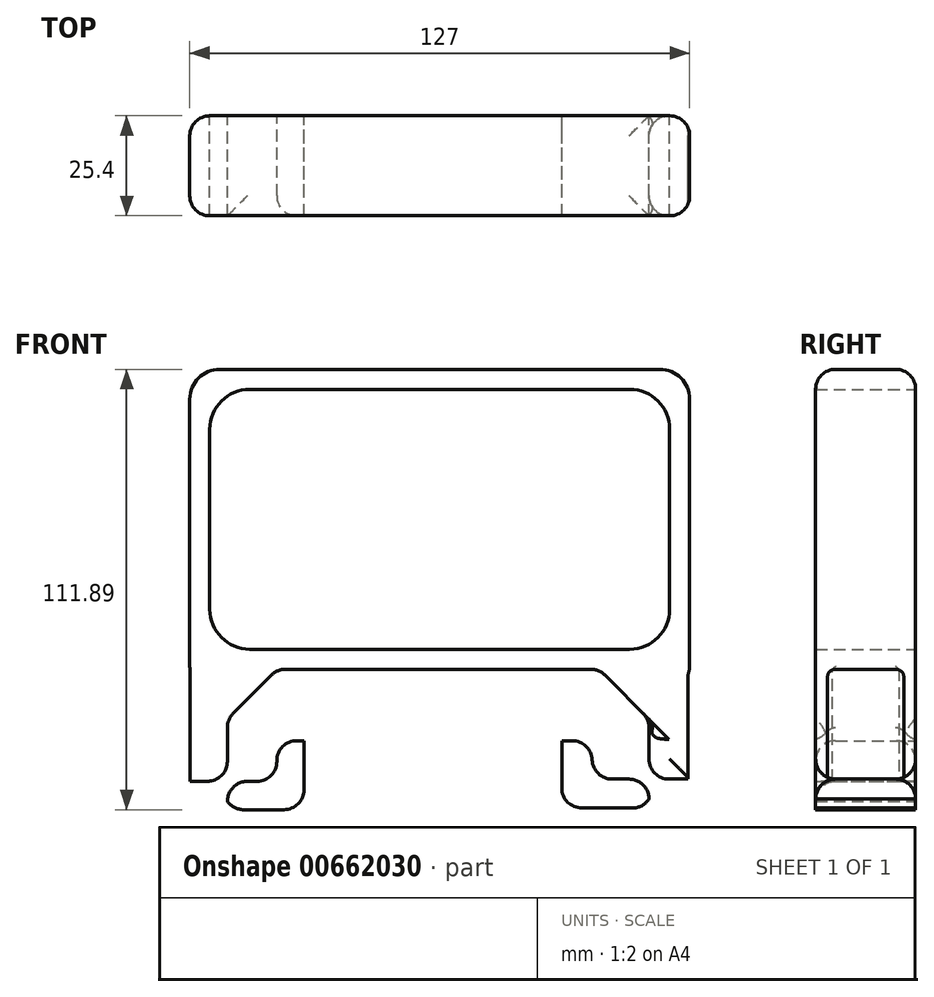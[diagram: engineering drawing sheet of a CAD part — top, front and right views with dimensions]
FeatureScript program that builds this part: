
annotation { "Feature Type Name" : "Feature", "Feature Type Description" : "" }
export const myFeature = defineFeature(function(context is Context, id is Id, definition is map)
    precondition{}
    {
        {
            var Q0;
            Q0=qCreatedBy(makeId("Front.planeOp"),FACE);
            var sketch = newSketch(context, id + "F0", { "sketchPlane" : qUnion([Q0])});
            skLineSegment(sketch, "E0.bottom", {"start": v(-63.5, 38.1) * mm, "end": v(63.5, 38.1) * mm});
            skLineSegment(sketch, "E0.top", {"start": v(-63.5, -38.1) * mm, "end": v(63.5, -38.1) * mm});
            skLineSegment(sketch, "E0.left", {"start": v(-63.5, 38.1) * mm, "end": v(-63.5, -38.1) * mm});
            skLineSegment(sketch, "E0.right", {"start": v(63.5, 38.1) * mm, "end": v(63.5, -38.1) * mm});
            skPoint(sketch, "E0.middle", {"position": v(0, 0) * mm});
            skSolve(sketch);
        }
        {
            var Q0;
            Q0=makeQuery(id+"F0.imprint","IMPRINT",FACE,{"disambiguationData":[TD([[makeQuery(id+"F0.imprint","IMPRINT",EDGE,{"derivedFrom":sQuery(id+"F0.wireOp",EDGE,"E0.bottom")}),-1.0]])]});
            extrude(context, id + "F1", {"entities" : qUnion([Q0]), "depth" : 25.4 * mm, "offsetDistance" : 25.4 * mm});
        }
        {
            var Q0;
            Q0=makeQuery(id+"F1.opExtrude","CAP_FACE",FACE,{"disambiguationData":[OSD([sQuery(id+"F0.wireOp",EDGE,"E0.bottom"),sQuery(id+"F0.wireOp",EDGE,"E0.top"),sQuery(id+"F0.wireOp",EDGE,"E0.left"),sQuery(id+"F0.wireOp",EDGE,"E0.right")])],"isStart":false});
            var Q1;
            Q1=makeQuery(id+"F1.opExtrude","CAP_FACE",FACE,{"disambiguationData":[OSD([sQuery(id+"F0.wireOp",EDGE,"E0.bottom"),sQuery(id+"F0.wireOp",EDGE,"E0.top"),sQuery(id+"F0.wireOp",EDGE,"E0.left"),sQuery(id+"F0.wireOp",EDGE,"E0.right")])],"isStart":true});
            shell(context, id + "F2", {"entities" : qUnion([Q0, Q1]), "thickness" : 5.08 * mm});
        }
        {
            var Q0;
            Q0=qCreatedBy(makeId("Front.planeOp"),FACE);
            var sketch = newSketch(context, id + "F3", { "sketchPlane" : qUnion([Q0])});
            skLineSegment(sketch, "E1.bottom", {"start": v(-63.44, -73.8) * mm, "end": v(-53.95, -73.8) * mm});
            skLineSegment(sketch, "E1.top", {"start": v(-63.44, -36.5) * mm, "end": v(-53.95, -36.5) * mm});
            skLineSegment(sketch, "E1.left", {"start": v(-63.44, -73.8) * mm, "end": v(-63.44, -36.5) * mm});
            skLineSegment(sketch, "E1.right", {"start": v(-53.95, -73.8) * mm, "end": v(-53.95, -36.5) * mm});
            skPoint(sketch, "E1.middle", {"position": v(-58.7, -55.14) * mm});
            skLineSegment(sketch, "E2.bottom", {"start": v(53.16, -73.37) * mm, "end": v(63.05, -73.37) * mm});
            skLineSegment(sketch, "E2.top", {"start": v(53.16, -36.3) * mm, "end": v(63.05, -36.3) * mm});
            skLineSegment(sketch, "E2.left", {"start": v(53.16, -73.37) * mm, "end": v(53.16, -36.3) * mm});
            skLineSegment(sketch, "E2.right", {"start": v(63.05, -73.37) * mm, "end": v(63.05, -36.3) * mm});
            skPoint(sketch, "E2.middle", {"position": v(58.1, -54.84) * mm});
            skLineSegment(sketch, "E3.bottom", {"start": v(-4.61, -73.37) * mm, "end": v(4.61, -73.37) * mm});
            skLineSegment(sketch, "E3.top", {"start": v(-4.61, -35.06) * mm, "end": v(4.61, -35.06) * mm});
            skPoint(sketch, "E3.middle", {"position": v(0, -54.22) * mm});
            skLineSegment(sketch, "E4.bottom", {"start": v(-63.44, -73.8) * mm, "end": v(-41.38, -73.8) * mm});
            skLineSegment(sketch, "E4.top", {"start": v(-63.44, -66.57) * mm, "end": v(-41.38, -66.57) * mm});
            skLineSegment(sketch, "E4.left", {"start": v(-63.44, -73.8) * mm, "end": v(-63.44, -66.57) * mm});
            skLineSegment(sketch, "E4.right", {"start": v(-41.38, -73.8) * mm, "end": v(-41.38, -66.57) * mm});
            skLineSegment(sketch, "E5.bottom", {"start": v(-4.61, -73.37) * mm, "end": v(20.81, -73.37) * mm});
            skLineSegment(sketch, "E5.left", {"start": v(-4.61, -73.37) * mm, "end": v(-4.61, -66.02) * mm});
            skLineSegment(sketch, "E5.right", {"start": v(20.81, -73.37) * mm, "end": v(20.81, -66.02) * mm});
            skLineSegment(sketch, "E6.bottom", {"start": v(63.05, -73.37) * mm, "end": v(38.73, -73.37) * mm});
            skLineSegment(sketch, "E6.top", {"start": v(63.05, -66.02) * mm, "end": v(38.73, -66.02) * mm});
            skLineSegment(sketch, "E6.left", {"start": v(63.05, -73.37) * mm, "end": v(63.05, -66.02) * mm});
            skLineSegment(sketch, "E6.right", {"start": v(38.73, -73.37) * mm, "end": v(38.73, -66.02) * mm});
            skLineSegment(sketch, "E7.bottom", {"start": v(-41.38, -73.8) * mm, "end": v(-34.49, -73.8) * mm});
            skLineSegment(sketch, "E7.top", {"start": v(-41.38, -56.28) * mm, "end": v(-34.49, -56.28) * mm});
            skLineSegment(sketch, "E7.left", {"start": v(-41.38, -73.8) * mm, "end": v(-41.38, -56.28) * mm});
            skLineSegment(sketch, "E7.right", {"start": v(-34.49, -73.8) * mm, "end": v(-34.49, -56.28) * mm});
            skLineSegment(sketch, "E8.bottom", {"start": v(38.73, -73.37) * mm, "end": v(31, -73.37) * mm});
            skLineSegment(sketch, "E8.top", {"start": v(38.73, -56.28) * mm, "end": v(31, -56.28) * mm});
            skLineSegment(sketch, "E8.left", {"start": v(38.73, -73.37) * mm, "end": v(38.73, -56.28) * mm});
            skLineSegment(sketch, "E8.right", {"start": v(31, -73.37) * mm, "end": v(31, -56.28) * mm});
            skSolve(sketch);
        }
        {
            var Q0;
            {var subQ0=sQuery(id+"F3.wireOp",EDGE,"E1.top");Q0=makeQuery(id+"F3.imprint","IMPRINT",FACE,{"disambiguationData":[TD([[makeQuery(id+"F3.imprint","IMPRINT",EDGE,{"derivedFrom":subQ0}),-1.0]])]});}
            var Q1;
            {var subQ5=sQuery(id+"F3.wireOp",EDGE,"E4.left");Q1=makeQuery(id+"F3.imprint","IMPRINT",FACE,{"disambiguationData":[TD([[makeQuery(id+"F3.imprint","IMPRINT",EDGE,{"derivedFrom":subQ5}),-1.0]])]});}
            var Q2;
            {var subQ0=sQuery(id+"F3.wireOp",EDGE,"E4.bottom");var subQ1=sQuery(id+"F3.wireOp",EDGE,"E1.right");var subQ2=makeQuery(id+"F3.imprint","INTERSECT",VERTEX,{"derivedFrom":[subQ1,subQ0]});Q2=makeQuery(id+"F3.imprint","IMPRINT",FACE,{"disambiguationData":[TD([[makeQuery(id+"F3.imprint","IMPRINT",EDGE,{"disambiguationData":[TD([[subQ2,-1.0]])],"derivedFrom":subQ1}),-1.0]])]});}
            var Q3;
            {var subQ3=sQuery(id+"F3.wireOp",EDGE,"E7.bottom");Q3=makeQuery(id+"F3.imprint","IMPRINT",FACE,{"disambiguationData":[TD([[makeQuery(id+"F3.imprint","IMPRINT",EDGE,{"derivedFrom":subQ3}),1.0]])]});}
            var Q4;
            {var subQ3=sQuery(id+"F3.wireOp",EDGE,"E8.bottom");Q4=makeQuery(id+"F3.imprint","IMPRINT",FACE,{"disambiguationData":[TD([[makeQuery(id+"F3.imprint","IMPRINT",EDGE,{"derivedFrom":subQ3}),-1.0]])]});}
            var Q5;
            {var subQ0=sQuery(id+"F3.wireOp",EDGE,"E6.bottom");var subQ1=sQuery(id+"F3.wireOp",EDGE,"E2.left");var subQ2=makeQuery(id+"F3.imprint","INTERSECT",VERTEX,{"derivedFrom":[subQ1,subQ0]});Q5=makeQuery(id+"F3.imprint","IMPRINT",FACE,{"disambiguationData":[TD([[makeQuery(id+"F3.imprint","IMPRINT",EDGE,{"disambiguationData":[TD([[subQ2,-1.0]])],"derivedFrom":subQ1}),1.0]])]});}
            var Q6;
            {var subQ5=sQuery(id+"F3.wireOp",EDGE,"E6.left");Q6=makeQuery(id+"F3.imprint","IMPRINT",FACE,{"disambiguationData":[TD([[makeQuery(id+"F3.imprint","IMPRINT",EDGE,{"derivedFrom":subQ5}),1.0]])]});}
            var Q7;
            {var subQ0=sQuery(id+"F3.wireOp",EDGE,"E2.top");Q7=makeQuery(id+"F3.imprint","IMPRINT",FACE,{"disambiguationData":[TD([[makeQuery(id+"F3.imprint","IMPRINT",EDGE,{"derivedFrom":subQ0}),-1.0]])]});}
            extrude(context, id + "F4", {"entities" : qUnion([Q0, Q1, Q2, Q3, Q4, Q5, Q6, Q7]), "operationType" : NewBodyOperationType.ADD, "depth" : 25.4 * mm, "offsetDistance" : 25.4 * mm});
        }
        {
            var Q0;
            Q0=makeQuery(id+"F4.boolean.opBoolean","INTERSECT",EDGE,{"derivedFrom":[makeQuery(id+"F1.opExtrude","SWEPT_FACE",FACE,{"disambiguationData":[OSD([sQuery(id+"F0.wireOp",EDGE,"E0.top")])]}),makeQuery(id+"F4.opExtrude","SWEPT_FACE",FACE,{"disambiguationData":[OSD([sQuery(id+"F3.wireOp",EDGE,"E2.right"),sQuery(id+"F3.wireOp",EDGE,"E6.left")])]})]});
            var Q1;
            Q1=makeQuery(id+"F1.opExtrude","SWEPT_EDGE",EDGE,{"disambiguationData":[OSD([sQuery(id+"F0.wireOp",EDGE,"E0.top"),sQuery(id+"F0.wireOp",EDGE,"E0.left")])]});
            fillet(context, id + "F5", {"entities" : qUnion([Q0, Q1]), "radius" : 5.08 * mm, "tangentPropagation" : true, "allowEdgeOverflow" : false});
        }
        {
            var Q0;
            Q0=makeQuery(id+"F4.boolean.opBoolean","INTERSECT",EDGE,{"derivedFrom":[makeQuery(id+"F1.opExtrude","SWEPT_FACE",FACE,{"disambiguationData":[OSD([sQuery(id+"F0.wireOp",EDGE,"E0.top")])]}),makeQuery(id+"F4.opExtrude","SWEPT_FACE",FACE,{"disambiguationData":[OSD([sQuery(id+"F3.wireOp",EDGE,"E2.left")])]})]});
            var Q1;
            Q1=makeQuery(id+"F4.boolean.opBoolean","INTERSECT",EDGE,{"derivedFrom":[makeQuery(id+"F1.opExtrude","SWEPT_FACE",FACE,{"disambiguationData":[OSD([sQuery(id+"F0.wireOp",EDGE,"E0.top")])]}),makeQuery(id+"F4.opExtrude","SWEPT_FACE",FACE,{"disambiguationData":[OSD([sQuery(id+"F3.wireOp",EDGE,"E1.right")])]})]});
            chamfer(context, id + "F6", {"entities" : qUnion([Q0, Q1]), "width" : 12.7 * mm, "tangentPropagation" : true});
        }
        {
            var Q0;
            Q0=makeQuery(id+"F4.opExtrude","SWEPT_EDGE",EDGE,{"disambiguationData":[OSD([sQuery(id+"F3.wireOp",EDGE,"E8.top"),sQuery(id+"F3.wireOp",EDGE,"E8.left")])]});
            var Q1;
            Q1=makeQuery(id+"F4.opExtrude","SWEPT_EDGE",EDGE,{"disambiguationData":[OSD([sQuery(id+"F3.wireOp",EDGE,"E7.top"),sQuery(id+"F3.wireOp",EDGE,"E7.left")])]});
            var Q2;
            Q2=makeQuery(id+"F4.opExtrude","SWEPT_EDGE",EDGE,{"disambiguationData":[OSD([sQuery(id+"F3.wireOp",EDGE,"E4.top"),sQuery(id+"F3.wireOp",EDGE,"E7.left")])]});
            var Q3;
            Q3=makeQuery(id+"F4.opExtrude","SWEPT_EDGE",EDGE,{"disambiguationData":[OSD([sQuery(id+"F3.wireOp",EDGE,"E1.right"),sQuery(id+"F3.wireOp",EDGE,"E4.top")])]});
            fillet(context, id + "F7", {"entities" : qUnion([Q0, Q1, Q2, Q3]), "radius" : 5.08 * mm, "tangentPropagation" : true, "allowEdgeOverflow" : false});
        }
        {
            var Q0;
            Q0=makeQuery(id+"F4.opExtrude","SWEPT_EDGE",EDGE,{"disambiguationData":[OSD([sQuery(id+"F3.wireOp",EDGE,"E2.left"),sQuery(id+"F3.wireOp",EDGE,"E6.top")])]});
            var Q1;
            Q1=makeQuery(id+"F4.opExtrude","SWEPT_EDGE",EDGE,{"disambiguationData":[OSD([sQuery(id+"F3.wireOp",EDGE,"E6.top"),sQuery(id+"F3.wireOp",EDGE,"E8.left")])]});
            fillet(context, id + "F8", {"entities" : qUnion([Q0, Q1]), "radius" : 5.08 * mm, "tangentPropagation" : true, "allowEdgeOverflow" : false});
        }
        {
            var Q0;
            Q0=makeQuery(id+"F4.opExtrude","SWEPT_EDGE",EDGE,{"disambiguationData":[OSD([sQuery(id+"F3.wireOp",EDGE,"E6.bottom"),sQuery(id+"F3.wireOp",EDGE,"E6.left")])]});
            var Q1;
            Q1=makeQuery(id+"F4.opExtrude","SWEPT_EDGE",EDGE,{"disambiguationData":[OSD([sQuery(id+"F3.wireOp",EDGE,"E4.bottom"),sQuery(id+"F3.wireOp",EDGE,"E4.left")])]});
            var Q2;
            Q2=makeQuery(id+"F4.opExtrude","SWEPT_EDGE",EDGE,{"disambiguationData":[OSD([sQuery(id+"F3.wireOp",EDGE,"E7.bottom"),sQuery(id+"F3.wireOp",EDGE,"E7.right")])]});
            var Q3;
            Q3=makeQuery(id+"F4.opExtrude","SWEPT_EDGE",EDGE,{"disambiguationData":[OSD([sQuery(id+"F3.wireOp",EDGE,"E8.bottom"),sQuery(id+"F3.wireOp",EDGE,"E8.right")])]});
            fillet(context, id + "F9", {"entities" : qUnion([Q0, Q1, Q2, Q3]), "radius" : 5.08 * mm, "tangentPropagation" : true, "allowEdgeOverflow" : false});
        }
        {
            var Q0;
            Q0=makeQuery(id+"F2.opShell","OFFSET_EDGE",EDGE,{"disambiguationData":[OSD([sQuery(id+"F0.wireOp",EDGE,"E0.bottom"),sQuery(id+"F0.wireOp",EDGE,"E0.left")])]});
            var Q1;
            Q1=makeQuery(id+"F2.opShell","OFFSET_EDGE",EDGE,{"disambiguationData":[OSD([sQuery(id+"F0.wireOp",EDGE,"E0.top"),sQuery(id+"F0.wireOp",EDGE,"E0.left")])]});
            var Q2;
            Q2=makeQuery(id+"F2.opShell","OFFSET_EDGE",EDGE,{"disambiguationData":[OSD([sQuery(id+"F0.wireOp",EDGE,"E0.top"),sQuery(id+"F0.wireOp",EDGE,"E0.right")])]});
            var Q3;
            Q3=makeQuery(id+"F2.opShell","OFFSET_EDGE",EDGE,{"disambiguationData":[OSD([sQuery(id+"F0.wireOp",EDGE,"E0.bottom"),sQuery(id+"F0.wireOp",EDGE,"E0.right")])]});
            fillet(context, id + "F10", {"entities" : qUnion([Q0, Q1, Q2, Q3]), "radius" : 10.16 * mm, "tangentPropagation" : true, "allowEdgeOverflow" : false});
        }
        {
            var Q0;
            Q0=makeQuery(id+"F1.opExtrude","SWEPT_EDGE",EDGE,{"disambiguationData":[OSD([sQuery(id+"F0.wireOp",EDGE,"E0.bottom"),sQuery(id+"F0.wireOp",EDGE,"E0.right")])]});
            var Q1;
            Q1=makeQuery(id+"F1.opExtrude","SWEPT_EDGE",EDGE,{"disambiguationData":[OSD([sQuery(id+"F0.wireOp",EDGE,"E0.bottom"),sQuery(id+"F0.wireOp",EDGE,"E0.left")])]});
            fillet(context, id + "F11", {"entities" : qUnion([Q0, Q1]), "radius" : 7.62 * mm, "tangentPropagation" : true, "allowEdgeOverflow" : false});
        }
        {
            var Q0;
            Q0=makeQuery(id+"F1.opExtrude","CAP_EDGE",EDGE,{"disambiguationData":[OSD([sQuery(id+"F0.wireOp",EDGE,"E0.bottom")])],"isStart":true});
            var Q1;
            Q1=makeQuery(id+"F1.opExtrude","CAP_EDGE",EDGE,{"disambiguationData":[OSD([sQuery(id+"F0.wireOp",EDGE,"E0.bottom")])],"isStart":false});
            fillet(context, id + "F12", {"entities" : qUnion([Q0, Q1]), "radius" : 5.08 * mm, "tangentPropagation" : true, "allowEdgeOverflow" : false});
        }
        {
            var Q0;
            {var subQ0=sQuery(id+"F3.wireOp",EDGE,"E8.left");var subQ1=sQuery(id+"F3.wireOp",EDGE,"E6.top");Q0=makeQuery(id+"F8.opFillet","BLEND_EDGE",EDGE,{"blendedFrom":[makeQuery(id+"F4.opExtrude","SWEPT_EDGE",EDGE,{"disambiguationData":[OSD([subQ1,subQ0])]}),makeQuery(id+"F4.boolean.opBoolean","MERGE",FACE,{"derivedFrom":[makeQuery(id+"F1.opExtrude","CAP_FACE",FACE,{"disambiguationData":[OSD([sQuery(id+"F0.wireOp",EDGE,"E0.bottom"),sQuery(id+"F0.wireOp",EDGE,"E0.top"),sQuery(id+"F0.wireOp",EDGE,"E0.left"),sQuery(id+"F0.wireOp",EDGE,"E0.right")])],"isStart":false}),makeQuery(id+"F4.opExtrude","CAP_FACE",FACE,{"disambiguationData":[OSD([sQuery(id+"F3.wireOp",EDGE,"E1.top"),sQuery(id+"F3.wireOp",EDGE,"E1.left"),sQuery(id+"F3.wireOp",EDGE,"E1.right"),sQuery(id+"F3.wireOp",EDGE,"E4.bottom"),sQuery(id+"F3.wireOp",EDGE,"E4.top"),sQuery(id+"F3.wireOp",EDGE,"E4.left"),sQuery(id+"F3.wireOp",EDGE,"E7.bottom"),sQuery(id+"F3.wireOp",EDGE,"E7.top"),sQuery(id+"F3.wireOp",EDGE,"E7.left"),sQuery(id+"F3.wireOp",EDGE,"E7.right")])],"isStart":false}),makeQuery(id+"F4.opExtrude","CAP_FACE",FACE,{"disambiguationData":[OSD([sQuery(id+"F3.wireOp",EDGE,"E2.top"),sQuery(id+"F3.wireOp",EDGE,"E2.left"),sQuery(id+"F3.wireOp",EDGE,"E2.right"),sQuery(id+"F3.wireOp",EDGE,"E6.bottom"),subQ1,sQuery(id+"F3.wireOp",EDGE,"E6.left"),sQuery(id+"F3.wireOp",EDGE,"E8.bottom"),sQuery(id+"F3.wireOp",EDGE,"E8.top"),subQ0,sQuery(id+"F3.wireOp",EDGE,"E8.right")])],"isStart":false})]})],"blendedInto":[makeQuery(id+"F4.boolean.opBoolean","MERGE",FACE,{"derivedFrom":[makeQuery(id+"F1.opExtrude","CAP_FACE",FACE,{"disambiguationData":[OSD([sQuery(id+"F0.wireOp",EDGE,"E0.bottom"),sQuery(id+"F0.wireOp",EDGE,"E0.top"),sQuery(id+"F0.wireOp",EDGE,"E0.left"),sQuery(id+"F0.wireOp",EDGE,"E0.right")])],"isStart":false}),makeQuery(id+"F4.opExtrude","CAP_FACE",FACE,{"disambiguationData":[OSD([sQuery(id+"F3.wireOp",EDGE,"E1.top"),sQuery(id+"F3.wireOp",EDGE,"E1.left"),sQuery(id+"F3.wireOp",EDGE,"E1.right"),sQuery(id+"F3.wireOp",EDGE,"E4.bottom"),sQuery(id+"F3.wireOp",EDGE,"E4.top"),sQuery(id+"F3.wireOp",EDGE,"E4.left"),sQuery(id+"F3.wireOp",EDGE,"E7.bottom"),sQuery(id+"F3.wireOp",EDGE,"E7.top"),sQuery(id+"F3.wireOp",EDGE,"E7.left"),sQuery(id+"F3.wireOp",EDGE,"E7.right")])],"isStart":false}),makeQuery(id+"F4.opExtrude","CAP_FACE",FACE,{"disambiguationData":[OSD([sQuery(id+"F3.wireOp",EDGE,"E2.top"),sQuery(id+"F3.wireOp",EDGE,"E2.left"),sQuery(id+"F3.wireOp",EDGE,"E2.right"),sQuery(id+"F3.wireOp",EDGE,"E6.bottom"),subQ1,sQuery(id+"F3.wireOp",EDGE,"E6.left"),sQuery(id+"F3.wireOp",EDGE,"E8.bottom"),sQuery(id+"F3.wireOp",EDGE,"E8.top"),subQ0,sQuery(id+"F3.wireOp",EDGE,"E8.right")])],"isStart":false})]})]});}
            var Q1;
            Q1=makeQuery(id+"F4.opExtrude","CAP_EDGE",EDGE,{"disambiguationData":[OSD([sQuery(id+"F3.wireOp",EDGE,"E6.top")])],"isStart":false});
            var Q2;
            {var subQ0=sQuery(id+"F3.wireOp",EDGE,"E6.top");var subQ1=sQuery(id+"F3.wireOp",EDGE,"E2.left");Q2=makeQuery(id+"F8.opFillet","BLEND_EDGE",EDGE,{"blendedFrom":[makeQuery(id+"F4.opExtrude","SWEPT_EDGE",EDGE,{"disambiguationData":[OSD([subQ1,subQ0])]}),makeQuery(id+"F4.boolean.opBoolean","MERGE",FACE,{"derivedFrom":[makeQuery(id+"F1.opExtrude","CAP_FACE",FACE,{"disambiguationData":[OSD([sQuery(id+"F0.wireOp",EDGE,"E0.bottom"),sQuery(id+"F0.wireOp",EDGE,"E0.top"),sQuery(id+"F0.wireOp",EDGE,"E0.left"),sQuery(id+"F0.wireOp",EDGE,"E0.right")])],"isStart":false}),makeQuery(id+"F4.opExtrude","CAP_FACE",FACE,{"disambiguationData":[OSD([sQuery(id+"F3.wireOp",EDGE,"E1.top"),sQuery(id+"F3.wireOp",EDGE,"E1.left"),sQuery(id+"F3.wireOp",EDGE,"E1.right"),sQuery(id+"F3.wireOp",EDGE,"E4.bottom"),sQuery(id+"F3.wireOp",EDGE,"E4.top"),sQuery(id+"F3.wireOp",EDGE,"E4.left"),sQuery(id+"F3.wireOp",EDGE,"E7.bottom"),sQuery(id+"F3.wireOp",EDGE,"E7.top"),sQuery(id+"F3.wireOp",EDGE,"E7.left"),sQuery(id+"F3.wireOp",EDGE,"E7.right")])],"isStart":false}),makeQuery(id+"F4.opExtrude","CAP_FACE",FACE,{"disambiguationData":[OSD([sQuery(id+"F3.wireOp",EDGE,"E2.top"),subQ1,sQuery(id+"F3.wireOp",EDGE,"E2.right"),sQuery(id+"F3.wireOp",EDGE,"E6.bottom"),subQ0,sQuery(id+"F3.wireOp",EDGE,"E6.left"),sQuery(id+"F3.wireOp",EDGE,"E8.bottom"),sQuery(id+"F3.wireOp",EDGE,"E8.top"),sQuery(id+"F3.wireOp",EDGE,"E8.left"),sQuery(id+"F3.wireOp",EDGE,"E8.right")])],"isStart":false})]})],"blendedInto":[makeQuery(id+"F4.boolean.opBoolean","MERGE",FACE,{"derivedFrom":[makeQuery(id+"F1.opExtrude","CAP_FACE",FACE,{"disambiguationData":[OSD([sQuery(id+"F0.wireOp",EDGE,"E0.bottom"),sQuery(id+"F0.wireOp",EDGE,"E0.top"),sQuery(id+"F0.wireOp",EDGE,"E0.left"),sQuery(id+"F0.wireOp",EDGE,"E0.right")])],"isStart":false}),makeQuery(id+"F4.opExtrude","CAP_FACE",FACE,{"disambiguationData":[OSD([sQuery(id+"F3.wireOp",EDGE,"E1.top"),sQuery(id+"F3.wireOp",EDGE,"E1.left"),sQuery(id+"F3.wireOp",EDGE,"E1.right"),sQuery(id+"F3.wireOp",EDGE,"E4.bottom"),sQuery(id+"F3.wireOp",EDGE,"E4.top"),sQuery(id+"F3.wireOp",EDGE,"E4.left"),sQuery(id+"F3.wireOp",EDGE,"E7.bottom"),sQuery(id+"F3.wireOp",EDGE,"E7.top"),sQuery(id+"F3.wireOp",EDGE,"E7.left"),sQuery(id+"F3.wireOp",EDGE,"E7.right")])],"isStart":false}),makeQuery(id+"F4.opExtrude","CAP_FACE",FACE,{"disambiguationData":[OSD([sQuery(id+"F3.wireOp",EDGE,"E2.top"),subQ1,sQuery(id+"F3.wireOp",EDGE,"E2.right"),sQuery(id+"F3.wireOp",EDGE,"E6.bottom"),subQ0,sQuery(id+"F3.wireOp",EDGE,"E6.left"),sQuery(id+"F3.wireOp",EDGE,"E8.bottom"),sQuery(id+"F3.wireOp",EDGE,"E8.top"),sQuery(id+"F3.wireOp",EDGE,"E8.left"),sQuery(id+"F3.wireOp",EDGE,"E8.right")])],"isStart":false})]})]});}
            var Q3;
            {var subQ0=sQuery(id+"F3.wireOp",EDGE,"E8.left");var subQ1=sQuery(id+"F3.wireOp",EDGE,"E6.top");Q3=makeQuery(id+"F8.opFillet","BLEND_EDGE",EDGE,{"blendedFrom":[makeQuery(id+"F4.opExtrude","SWEPT_EDGE",EDGE,{"disambiguationData":[OSD([subQ1,subQ0])]}),makeQuery(id+"F4.boolean.opBoolean","MERGE",FACE,{"derivedFrom":[makeQuery(id+"F1.opExtrude","CAP_FACE",FACE,{"disambiguationData":[OSD([sQuery(id+"F0.wireOp",EDGE,"E0.bottom"),sQuery(id+"F0.wireOp",EDGE,"E0.top"),sQuery(id+"F0.wireOp",EDGE,"E0.left"),sQuery(id+"F0.wireOp",EDGE,"E0.right")])],"isStart":true}),makeQuery(id+"F4.opExtrude","CAP_FACE",FACE,{"disambiguationData":[OSD([sQuery(id+"F3.wireOp",EDGE,"E1.top"),sQuery(id+"F3.wireOp",EDGE,"E1.left"),sQuery(id+"F3.wireOp",EDGE,"E1.right"),sQuery(id+"F3.wireOp",EDGE,"E4.bottom"),sQuery(id+"F3.wireOp",EDGE,"E4.top"),sQuery(id+"F3.wireOp",EDGE,"E4.left"),sQuery(id+"F3.wireOp",EDGE,"E7.bottom"),sQuery(id+"F3.wireOp",EDGE,"E7.top"),sQuery(id+"F3.wireOp",EDGE,"E7.left"),sQuery(id+"F3.wireOp",EDGE,"E7.right")])],"isStart":true}),makeQuery(id+"F4.opExtrude","CAP_FACE",FACE,{"disambiguationData":[OSD([sQuery(id+"F3.wireOp",EDGE,"E2.top"),sQuery(id+"F3.wireOp",EDGE,"E2.left"),sQuery(id+"F3.wireOp",EDGE,"E2.right"),sQuery(id+"F3.wireOp",EDGE,"E6.bottom"),subQ1,sQuery(id+"F3.wireOp",EDGE,"E6.left"),sQuery(id+"F3.wireOp",EDGE,"E8.bottom"),sQuery(id+"F3.wireOp",EDGE,"E8.top"),subQ0,sQuery(id+"F3.wireOp",EDGE,"E8.right")])],"isStart":true})]})],"blendedInto":[makeQuery(id+"F4.boolean.opBoolean","MERGE",FACE,{"derivedFrom":[makeQuery(id+"F1.opExtrude","CAP_FACE",FACE,{"disambiguationData":[OSD([sQuery(id+"F0.wireOp",EDGE,"E0.bottom"),sQuery(id+"F0.wireOp",EDGE,"E0.top"),sQuery(id+"F0.wireOp",EDGE,"E0.left"),sQuery(id+"F0.wireOp",EDGE,"E0.right")])],"isStart":true}),makeQuery(id+"F4.opExtrude","CAP_FACE",FACE,{"disambiguationData":[OSD([sQuery(id+"F3.wireOp",EDGE,"E1.top"),sQuery(id+"F3.wireOp",EDGE,"E1.left"),sQuery(id+"F3.wireOp",EDGE,"E1.right"),sQuery(id+"F3.wireOp",EDGE,"E4.bottom"),sQuery(id+"F3.wireOp",EDGE,"E4.top"),sQuery(id+"F3.wireOp",EDGE,"E4.left"),sQuery(id+"F3.wireOp",EDGE,"E7.bottom"),sQuery(id+"F3.wireOp",EDGE,"E7.top"),sQuery(id+"F3.wireOp",EDGE,"E7.left"),sQuery(id+"F3.wireOp",EDGE,"E7.right")])],"isStart":true}),makeQuery(id+"F4.opExtrude","CAP_FACE",FACE,{"disambiguationData":[OSD([sQuery(id+"F3.wireOp",EDGE,"E2.top"),sQuery(id+"F3.wireOp",EDGE,"E2.left"),sQuery(id+"F3.wireOp",EDGE,"E2.right"),sQuery(id+"F3.wireOp",EDGE,"E6.bottom"),subQ1,sQuery(id+"F3.wireOp",EDGE,"E6.left"),sQuery(id+"F3.wireOp",EDGE,"E8.bottom"),sQuery(id+"F3.wireOp",EDGE,"E8.top"),subQ0,sQuery(id+"F3.wireOp",EDGE,"E8.right")])],"isStart":true})]})]});}
            var Q4;
            Q4=makeQuery(id+"F4.opExtrude","CAP_EDGE",EDGE,{"disambiguationData":[OSD([sQuery(id+"F3.wireOp",EDGE,"E6.top")])],"isStart":true});
            fillet(context, id + "F13", {"entities" : qUnion([Q0, Q1, Q2, Q3, Q4]), "radius" : 5.08 * mm, "tangentPropagation" : true, "allowEdgeOverflow" : false});
        }
        {
            var Q0;
            {var subQ0=sQuery(id+"F3.wireOp",EDGE,"E7.left");var subQ1=sQuery(id+"F3.wireOp",EDGE,"E4.top");Q0=makeQuery(id+"F7.opFillet","BLEND_EDGE",EDGE,{"blendedFrom":[makeQuery(id+"F4.opExtrude","SWEPT_EDGE",EDGE,{"disambiguationData":[OSD([subQ1,subQ0])]}),makeQuery(id+"F4.boolean.opBoolean","MERGE",FACE,{"derivedFrom":[makeQuery(id+"F1.opExtrude","CAP_FACE",FACE,{"disambiguationData":[OSD([sQuery(id+"F0.wireOp",EDGE,"E0.bottom"),sQuery(id+"F0.wireOp",EDGE,"E0.top"),sQuery(id+"F0.wireOp",EDGE,"E0.left"),sQuery(id+"F0.wireOp",EDGE,"E0.right")])],"isStart":false}),makeQuery(id+"F4.opExtrude","CAP_FACE",FACE,{"disambiguationData":[OSD([sQuery(id+"F3.wireOp",EDGE,"E1.top"),sQuery(id+"F3.wireOp",EDGE,"E1.left"),sQuery(id+"F3.wireOp",EDGE,"E1.right"),sQuery(id+"F3.wireOp",EDGE,"E4.bottom"),subQ1,sQuery(id+"F3.wireOp",EDGE,"E4.left"),sQuery(id+"F3.wireOp",EDGE,"E7.bottom"),sQuery(id+"F3.wireOp",EDGE,"E7.top"),subQ0,sQuery(id+"F3.wireOp",EDGE,"E7.right")])],"isStart":false}),makeQuery(id+"F4.opExtrude","CAP_FACE",FACE,{"disambiguationData":[OSD([sQuery(id+"F3.wireOp",EDGE,"E2.top"),sQuery(id+"F3.wireOp",EDGE,"E2.left"),sQuery(id+"F3.wireOp",EDGE,"E2.right"),sQuery(id+"F3.wireOp",EDGE,"E6.bottom"),sQuery(id+"F3.wireOp",EDGE,"E6.top"),sQuery(id+"F3.wireOp",EDGE,"E6.left"),sQuery(id+"F3.wireOp",EDGE,"E8.bottom"),sQuery(id+"F3.wireOp",EDGE,"E8.top"),sQuery(id+"F3.wireOp",EDGE,"E8.left"),sQuery(id+"F3.wireOp",EDGE,"E8.right")])],"isStart":false})]})],"blendedInto":[makeQuery(id+"F4.boolean.opBoolean","MERGE",FACE,{"derivedFrom":[makeQuery(id+"F1.opExtrude","CAP_FACE",FACE,{"disambiguationData":[OSD([sQuery(id+"F0.wireOp",EDGE,"E0.bottom"),sQuery(id+"F0.wireOp",EDGE,"E0.top"),sQuery(id+"F0.wireOp",EDGE,"E0.left"),sQuery(id+"F0.wireOp",EDGE,"E0.right")])],"isStart":false}),makeQuery(id+"F4.opExtrude","CAP_FACE",FACE,{"disambiguationData":[OSD([sQuery(id+"F3.wireOp",EDGE,"E1.top"),sQuery(id+"F3.wireOp",EDGE,"E1.left"),sQuery(id+"F3.wireOp",EDGE,"E1.right"),sQuery(id+"F3.wireOp",EDGE,"E4.bottom"),subQ1,sQuery(id+"F3.wireOp",EDGE,"E4.left"),sQuery(id+"F3.wireOp",EDGE,"E7.bottom"),sQuery(id+"F3.wireOp",EDGE,"E7.top"),subQ0,sQuery(id+"F3.wireOp",EDGE,"E7.right")])],"isStart":false}),makeQuery(id+"F4.opExtrude","CAP_FACE",FACE,{"disambiguationData":[OSD([sQuery(id+"F3.wireOp",EDGE,"E2.top"),sQuery(id+"F3.wireOp",EDGE,"E2.left"),sQuery(id+"F3.wireOp",EDGE,"E2.right"),sQuery(id+"F3.wireOp",EDGE,"E6.bottom"),sQuery(id+"F3.wireOp",EDGE,"E6.top"),sQuery(id+"F3.wireOp",EDGE,"E6.left"),sQuery(id+"F3.wireOp",EDGE,"E8.bottom"),sQuery(id+"F3.wireOp",EDGE,"E8.top"),sQuery(id+"F3.wireOp",EDGE,"E8.left"),sQuery(id+"F3.wireOp",EDGE,"E8.right")])],"isStart":false})]})]});}
            var Q1;
            Q1=makeQuery(id+"F4.opExtrude","CAP_EDGE",EDGE,{"disambiguationData":[OSD([sQuery(id+"F3.wireOp",EDGE,"E4.top")])],"isStart":false});
            var Q2;
            {var subQ0=sQuery(id+"F3.wireOp",EDGE,"E4.top");var subQ1=sQuery(id+"F3.wireOp",EDGE,"E1.right");Q2=makeQuery(id+"F7.opFillet","BLEND_EDGE",EDGE,{"blendedFrom":[makeQuery(id+"F4.opExtrude","SWEPT_EDGE",EDGE,{"disambiguationData":[OSD([subQ1,subQ0])]}),makeQuery(id+"F4.boolean.opBoolean","MERGE",FACE,{"derivedFrom":[makeQuery(id+"F1.opExtrude","CAP_FACE",FACE,{"disambiguationData":[OSD([sQuery(id+"F0.wireOp",EDGE,"E0.bottom"),sQuery(id+"F0.wireOp",EDGE,"E0.top"),sQuery(id+"F0.wireOp",EDGE,"E0.left"),sQuery(id+"F0.wireOp",EDGE,"E0.right")])],"isStart":false}),makeQuery(id+"F4.opExtrude","CAP_FACE",FACE,{"disambiguationData":[OSD([sQuery(id+"F3.wireOp",EDGE,"E1.top"),sQuery(id+"F3.wireOp",EDGE,"E1.left"),subQ1,sQuery(id+"F3.wireOp",EDGE,"E4.bottom"),subQ0,sQuery(id+"F3.wireOp",EDGE,"E4.left"),sQuery(id+"F3.wireOp",EDGE,"E7.bottom"),sQuery(id+"F3.wireOp",EDGE,"E7.top"),sQuery(id+"F3.wireOp",EDGE,"E7.left"),sQuery(id+"F3.wireOp",EDGE,"E7.right")])],"isStart":false}),makeQuery(id+"F4.opExtrude","CAP_FACE",FACE,{"disambiguationData":[OSD([sQuery(id+"F3.wireOp",EDGE,"E2.top"),sQuery(id+"F3.wireOp",EDGE,"E2.left"),sQuery(id+"F3.wireOp",EDGE,"E2.right"),sQuery(id+"F3.wireOp",EDGE,"E6.bottom"),sQuery(id+"F3.wireOp",EDGE,"E6.top"),sQuery(id+"F3.wireOp",EDGE,"E6.left"),sQuery(id+"F3.wireOp",EDGE,"E8.bottom"),sQuery(id+"F3.wireOp",EDGE,"E8.top"),sQuery(id+"F3.wireOp",EDGE,"E8.left"),sQuery(id+"F3.wireOp",EDGE,"E8.right")])],"isStart":false})]})],"blendedInto":[makeQuery(id+"F4.boolean.opBoolean","MERGE",FACE,{"derivedFrom":[makeQuery(id+"F1.opExtrude","CAP_FACE",FACE,{"disambiguationData":[OSD([sQuery(id+"F0.wireOp",EDGE,"E0.bottom"),sQuery(id+"F0.wireOp",EDGE,"E0.top"),sQuery(id+"F0.wireOp",EDGE,"E0.left"),sQuery(id+"F0.wireOp",EDGE,"E0.right")])],"isStart":false}),makeQuery(id+"F4.opExtrude","CAP_FACE",FACE,{"disambiguationData":[OSD([sQuery(id+"F3.wireOp",EDGE,"E1.top"),sQuery(id+"F3.wireOp",EDGE,"E1.left"),subQ1,sQuery(id+"F3.wireOp",EDGE,"E4.bottom"),subQ0,sQuery(id+"F3.wireOp",EDGE,"E4.left"),sQuery(id+"F3.wireOp",EDGE,"E7.bottom"),sQuery(id+"F3.wireOp",EDGE,"E7.top"),sQuery(id+"F3.wireOp",EDGE,"E7.left"),sQuery(id+"F3.wireOp",EDGE,"E7.right")])],"isStart":false}),makeQuery(id+"F4.opExtrude","CAP_FACE",FACE,{"disambiguationData":[OSD([sQuery(id+"F3.wireOp",EDGE,"E2.top"),sQuery(id+"F3.wireOp",EDGE,"E2.left"),sQuery(id+"F3.wireOp",EDGE,"E2.right"),sQuery(id+"F3.wireOp",EDGE,"E6.bottom"),sQuery(id+"F3.wireOp",EDGE,"E6.top"),sQuery(id+"F3.wireOp",EDGE,"E6.left"),sQuery(id+"F3.wireOp",EDGE,"E8.bottom"),sQuery(id+"F3.wireOp",EDGE,"E8.top"),sQuery(id+"F3.wireOp",EDGE,"E8.left"),sQuery(id+"F3.wireOp",EDGE,"E8.right")])],"isStart":false})]})]});}
            var Q3;
            {var subQ0=sQuery(id+"F3.wireOp",EDGE,"E4.top");var subQ1=sQuery(id+"F3.wireOp",EDGE,"E1.right");Q3=makeQuery(id+"F7.opFillet","BLEND_EDGE",EDGE,{"blendedFrom":[makeQuery(id+"F4.opExtrude","SWEPT_EDGE",EDGE,{"disambiguationData":[OSD([subQ1,subQ0])]}),makeQuery(id+"F4.boolean.opBoolean","MERGE",FACE,{"derivedFrom":[makeQuery(id+"F1.opExtrude","CAP_FACE",FACE,{"disambiguationData":[OSD([sQuery(id+"F0.wireOp",EDGE,"E0.bottom"),sQuery(id+"F0.wireOp",EDGE,"E0.top"),sQuery(id+"F0.wireOp",EDGE,"E0.left"),sQuery(id+"F0.wireOp",EDGE,"E0.right")])],"isStart":true}),makeQuery(id+"F4.opExtrude","CAP_FACE",FACE,{"disambiguationData":[OSD([sQuery(id+"F3.wireOp",EDGE,"E1.top"),sQuery(id+"F3.wireOp",EDGE,"E1.left"),subQ1,sQuery(id+"F3.wireOp",EDGE,"E4.bottom"),subQ0,sQuery(id+"F3.wireOp",EDGE,"E4.left"),sQuery(id+"F3.wireOp",EDGE,"E7.bottom"),sQuery(id+"F3.wireOp",EDGE,"E7.top"),sQuery(id+"F3.wireOp",EDGE,"E7.left"),sQuery(id+"F3.wireOp",EDGE,"E7.right")])],"isStart":true}),makeQuery(id+"F4.opExtrude","CAP_FACE",FACE,{"disambiguationData":[OSD([sQuery(id+"F3.wireOp",EDGE,"E2.top"),sQuery(id+"F3.wireOp",EDGE,"E2.left"),sQuery(id+"F3.wireOp",EDGE,"E2.right"),sQuery(id+"F3.wireOp",EDGE,"E6.bottom"),sQuery(id+"F3.wireOp",EDGE,"E6.top"),sQuery(id+"F3.wireOp",EDGE,"E6.left"),sQuery(id+"F3.wireOp",EDGE,"E8.bottom"),sQuery(id+"F3.wireOp",EDGE,"E8.top"),sQuery(id+"F3.wireOp",EDGE,"E8.left"),sQuery(id+"F3.wireOp",EDGE,"E8.right")])],"isStart":true})]})],"blendedInto":[makeQuery(id+"F4.boolean.opBoolean","MERGE",FACE,{"derivedFrom":[makeQuery(id+"F1.opExtrude","CAP_FACE",FACE,{"disambiguationData":[OSD([sQuery(id+"F0.wireOp",EDGE,"E0.bottom"),sQuery(id+"F0.wireOp",EDGE,"E0.top"),sQuery(id+"F0.wireOp",EDGE,"E0.left"),sQuery(id+"F0.wireOp",EDGE,"E0.right")])],"isStart":true}),makeQuery(id+"F4.opExtrude","CAP_FACE",FACE,{"disambiguationData":[OSD([sQuery(id+"F3.wireOp",EDGE,"E1.top"),sQuery(id+"F3.wireOp",EDGE,"E1.left"),subQ1,sQuery(id+"F3.wireOp",EDGE,"E4.bottom"),subQ0,sQuery(id+"F3.wireOp",EDGE,"E4.left"),sQuery(id+"F3.wireOp",EDGE,"E7.bottom"),sQuery(id+"F3.wireOp",EDGE,"E7.top"),sQuery(id+"F3.wireOp",EDGE,"E7.left"),sQuery(id+"F3.wireOp",EDGE,"E7.right")])],"isStart":true}),makeQuery(id+"F4.opExtrude","CAP_FACE",FACE,{"disambiguationData":[OSD([sQuery(id+"F3.wireOp",EDGE,"E2.top"),sQuery(id+"F3.wireOp",EDGE,"E2.left"),sQuery(id+"F3.wireOp",EDGE,"E2.right"),sQuery(id+"F3.wireOp",EDGE,"E6.bottom"),sQuery(id+"F3.wireOp",EDGE,"E6.top"),sQuery(id+"F3.wireOp",EDGE,"E6.left"),sQuery(id+"F3.wireOp",EDGE,"E8.bottom"),sQuery(id+"F3.wireOp",EDGE,"E8.top"),sQuery(id+"F3.wireOp",EDGE,"E8.left"),sQuery(id+"F3.wireOp",EDGE,"E8.right")])],"isStart":true})]})]});}
            fillet(context, id + "F14", {"entities" : qUnion([Q0, Q1, Q2, Q3]), "radius" : 5.08 * mm, "tangentPropagation" : true, "allowEdgeOverflow" : false});
        }
        {
            var Q0;
            {var subQ7=sQuery(id+"F3.wireOp",EDGE,"E1.right");var subQ12=sQuery(id+"F0.wireOp",EDGE,"E0.top");var subQ14=sQuery(id+"F3.wireOp",EDGE,"E2.left");var subQ15=makeQuery(id+"F4.opExtrude","SWEPT_FACE",FACE,{"disambiguationData":[OSD([subQ14])]});var subQ25=makeQuery(id+"F1.opExtrude","SWEPT_FACE",FACE,{"disambiguationData":[OSD([subQ12])]});Q0=makeQuery(id+"F6.opChamfer","BLEND_EDGE",EDGE,{"blendedFrom":[makeQuery(id+"F4.boolean.opBoolean","INTERSECT",EDGE,{"derivedFrom":[subQ25,subQ15]}),makeQuery(id+"F4.boolean.opBoolean","SPLIT",FACE,{"disambiguationData":[TD([makeQuery(id+"F4.opExtrude","SWEPT_FACE",FACE,{"disambiguationData":[OSD([subQ7])]})])],"derivedFrom":subQ25})],"blendedInto":[makeQuery(id+"F4.boolean.opBoolean","SPLIT",FACE,{"disambiguationData":[TD([makeQuery(id+"F4.opExtrude","SWEPT_FACE",FACE,{"disambiguationData":[OSD([subQ7])]})])],"derivedFrom":subQ25})]});}
            var Q1;
            {var subQ7=sQuery(id+"F3.wireOp",EDGE,"E1.right");var subQ12=sQuery(id+"F0.wireOp",EDGE,"E0.top");var subQ24=makeQuery(id+"F4.opExtrude","SWEPT_FACE",FACE,{"disambiguationData":[OSD([subQ7])]});var subQ25=makeQuery(id+"F1.opExtrude","SWEPT_FACE",FACE,{"disambiguationData":[OSD([subQ12])]});Q1=makeQuery(id+"F6.opChamfer","BLEND_EDGE",EDGE,{"blendedFrom":[makeQuery(id+"F4.boolean.opBoolean","INTERSECT",EDGE,{"derivedFrom":[subQ25,subQ24]}),makeQuery(id+"F4.boolean.opBoolean","SPLIT",FACE,{"disambiguationData":[TD([subQ24])],"derivedFrom":subQ25})],"blendedInto":[makeQuery(id+"F4.boolean.opBoolean","SPLIT",FACE,{"disambiguationData":[TD([subQ24])],"derivedFrom":subQ25})]});}
            fillet(context, id + "F15", {"entities" : qUnion([Q0, Q1]), "radius" : 5.08 * mm, "tangentPropagation" : true, "allowEdgeOverflow" : false});
        }
        {
            var Q0;
            {var subQ0=makeQuery(id+"F4.opExtrude","SWEPT_FACE",FACE,{"disambiguationData":[OSD([sQuery(id+"F3.wireOp",EDGE,"E1.right")])]});Q0=makeQuery(id+"F6.opChamfer","BLEND_EDGE",EDGE,{"blendedFrom":[makeQuery(id+"F4.boolean.opBoolean","INTERSECT",EDGE,{"derivedFrom":[makeQuery(id+"F1.opExtrude","SWEPT_FACE",FACE,{"disambiguationData":[OSD([sQuery(id+"F0.wireOp",EDGE,"E0.top")])]}),subQ0]}),subQ0],"blendedInto":[subQ0]});}
            var Q1;
            {var subQ0=makeQuery(id+"F4.opExtrude","SWEPT_FACE",FACE,{"disambiguationData":[OSD([sQuery(id+"F3.wireOp",EDGE,"E2.left")])]});Q1=makeQuery(id+"F6.opChamfer","BLEND_EDGE",EDGE,{"blendedFrom":[makeQuery(id+"F4.boolean.opBoolean","INTERSECT",EDGE,{"derivedFrom":[makeQuery(id+"F1.opExtrude","SWEPT_FACE",FACE,{"disambiguationData":[OSD([sQuery(id+"F0.wireOp",EDGE,"E0.top")])]}),subQ0]}),subQ0],"blendedInto":[subQ0]});}
            fillet(context, id + "F16", {"entities" : qUnion([Q0, Q1]), "radius" : 5.08 * mm, "tangentPropagation" : true, "allowEdgeOverflow" : false});
        }
    });
